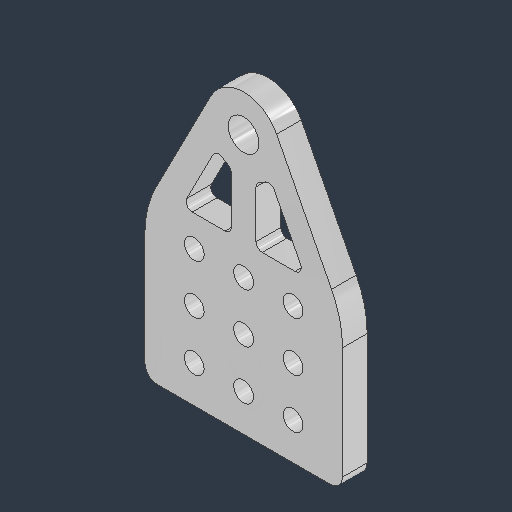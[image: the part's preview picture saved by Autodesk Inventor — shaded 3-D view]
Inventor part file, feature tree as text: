
AUTODESK INVENTOR PART (.ipt)
format: ipt  version: 2024.3 (Build 283343000, 343)  size: 284,160 bytes
history: native  units: in
note: dims shown in document units (in); Inventor stores cm internally (conversion verified against a paired STEP export)
features: fillet x3, sketch x3, hole x2, extrude x1
ambient origin geometry x8: Origin, YZ Plane, XZ Plane, XY Plane, X Axis, Y Axis, Z Axis, Center Point
bodies: Body1 (feature_tree)
feature tree (9):
  extrude  "Extrusion2"  Depth=1.0in
  hole  "Hole2"  [1 undecoded]
  hole  "Hole4"  [1 undecoded]
  fillet  "Fillet5"  Radius=0.3937in
  fillet  "Fillet7"  Radius=1.125in
  fillet  "Fillet9"  Radius=0.375in
  sketch  "Sketch1"  dims[d32=0.25in d33=0.0in d43=1.0in]
  sketch  "Sketch3"  dims[d45=0.125in]
  sketch  "Sketch7"  dims[d46=0.201in d47=0.38in d48=0.375in d49=0.19in d50=0.5635in d51=0.536in d52=0.8108in d64=0.125in d95=0.3125in d96=0.75in d97=0.375in d98=0.25in d99=0.5635in d100=1.0in d101=0.8108in d103=0.0625in d105=1.1811in d107=0.5in d108=0.3937in d110=1.0in d112=1.125in d113=0.375in d114=2.0in d115=1.5in d117=0.25in d118=0.1875in d119=0.25in d121=1.0in]
note: 2 required parameter values undecoded (feature->parameter linkage not recoverable at this tier; creation-order binding heuristic only, values carry confidence <= 0.55)
